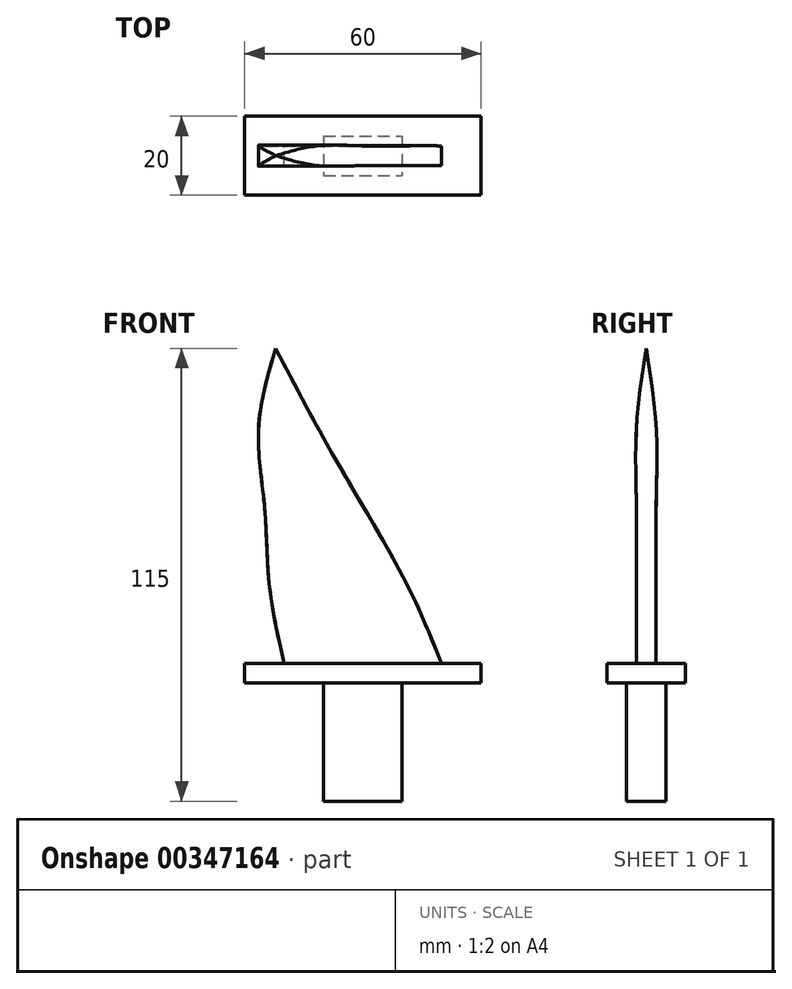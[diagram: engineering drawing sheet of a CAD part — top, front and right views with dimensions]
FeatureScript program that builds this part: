
annotation { "Feature Type Name" : "Feature", "Feature Type Description" : "" }
export const myFeature = defineFeature(function(context is Context, id is Id, definition is map)
    precondition{}
    {
        {
            var Q0;
            Q0=qCreatedBy(makeId("Top.planeOp"),FACE);
            var sketch = newSketch(context, id + "F0", { "sketchPlane" : qUnion([Q0])});
            skLineSegment(sketch, "E0.bottom", {"start": v(-10, 5) * mm, "end": v(10, 5) * mm});
            skLineSegment(sketch, "E0.top", {"start": v(-10, -5) * mm, "end": v(10, -5) * mm});
            skLineSegment(sketch, "E0.left", {"start": v(-10, 5) * mm, "end": v(-10, -5) * mm});
            skLineSegment(sketch, "E0.right", {"start": v(10, 5) * mm, "end": v(10, -5) * mm});
            skPoint(sketch, "E0.middle", {"position": v(0, 0) * mm});
            skSolve(sketch);
        }
        {
            var Q0;
            Q0=makeQuery(id+"F0.imprint","IMPRINT",FACE,{"disambiguationData":[TD([[makeQuery(id+"F0.imprint","IMPRINT",EDGE,{"derivedFrom":sQuery(id+"F0.wireOp",EDGE,"E0.bottom")}),-1.0]])]});
            extrude(context, id + "F1", {"entities" : qUnion([Q0]), "depth" : 30 * mm});
        }
        {
            var Q0;
            Q0=qCreatedBy(makeId("Top.planeOp"),FACE);
            cPlane(context, id + "F2", {"entities" : qUnion([Q0]), "cplaneType" : CPlaneType.OFFSET, "offset" : 30 * mm, "width" : 150 * mm, "height" : 150 * mm});
        }
        {
            var Q0;
            Q0=qCreatedBy(id+"F2.planeOp",FACE);
            var sketch = newSketch(context, id + "F3", { "sketchPlane" : qUnion([Q0])});
            skLineSegment(sketch, "E1.bottom", {"start": v(-30, 10) * mm, "end": v(30, 10) * mm});
            skLineSegment(sketch, "E1.top", {"start": v(-30, -10) * mm, "end": v(30, -10) * mm});
            skLineSegment(sketch, "E1.left", {"start": v(-30, 10) * mm, "end": v(-30, -10) * mm});
            skLineSegment(sketch, "E1.right", {"start": v(30, 10) * mm, "end": v(30, -10) * mm});
            skPoint(sketch, "E1.middle", {"position": v(0, 0) * mm});
            skSolve(sketch);
        }
        {
            var Q0;
            Q0=makeQuery(id+"F3.imprint","IMPRINT",FACE,{"disambiguationData":[TD([[makeQuery(id+"F3.imprint","IMPRINT",EDGE,{"derivedFrom":sQuery(id+"F3.wireOp",EDGE,"E1.bottom")}),-1.0]])]});
            extrude(context, id + "F4", {"entities" : qUnion([Q0]), "operationType" : NewBodyOperationType.ADD, "depth" : 5 * mm});
        }
        {
            var Q0;
            Q0=qCreatedBy(id+"F2.planeOp",FACE);
            cPlane(context, id + "F5", {"entities" : qUnion([Q0]), "cplaneType" : CPlaneType.OFFSET, "offset" : 5 * mm, "width" : 150 * mm, "height" : 150 * mm});
        }
        {
            var Q0;
            Q0=qCreatedBy(id+"F5.planeOp",FACE);
            var sketch = newSketch(context, id + "F6", { "sketchPlane" : qUnion([Q0])});
            skLineSegment(sketch, "E2.bottom", {"start": v(-20, -2.5) * mm, "end": v(20, -2.5) * mm});
            skLineSegment(sketch, "E2.top", {"start": v(-20, 2.5) * mm, "end": v(20, 2.5) * mm});
            skLineSegment(sketch, "E2.left", {"start": v(-20, -2.5) * mm, "end": v(-20, 2.5) * mm});
            skLineSegment(sketch, "E2.right", {"start": v(20, -2.5) * mm, "end": v(20, 2.5) * mm});
            skPoint(sketch, "E2.middle", {"position": v(0, 0) * mm});
            skSolve(sketch);
        }
        {
            var Q0;
            Q0=qCreatedBy(id+"F5.planeOp",FACE);
            cPlane(context, id + "F7", {"entities" : qUnion([Q0]), "cplaneType" : CPlaneType.OFFSET, "offset" : 20 * mm, "width" : 150 * mm, "height" : 150 * mm});
        }
        {
            var Q0;
            Q0=qCreatedBy(id+"F7.planeOp",FACE);
            var sketch = newSketch(context, id + "F8", { "sketchPlane" : qUnion([Q0])});
            skLineSegment(sketch, "E3.bottom", {"start": v(11.25, -2.5) * mm, "end": v(-23.75, -2.5) * mm});
            skLineSegment(sketch, "E3.top", {"start": v(11.25, 2.5) * mm, "end": v(-23.75, 2.5) * mm});
            skLineSegment(sketch, "E3.left", {"start": v(11.25, -2.5) * mm, "end": v(11.25, 2.5) * mm});
            skLineSegment(sketch, "E3.right", {"start": v(-23.75, -2.5) * mm, "end": v(-23.75, 2.5) * mm});
            skPoint(sketch, "E3.middle", {"position": v(-6.25, 0) * mm});
            skSolve(sketch);
        }
        {
            var Q0;
            Q0=qCreatedBy(id+"F7.planeOp",FACE);
            cPlane(context, id + "F9", {"entities" : qUnion([Q0]), "cplaneType" : CPlaneType.OFFSET, "offset" : 20 * mm, "width" : 150 * mm, "height" : 150 * mm});
        }
        {
            var Q0;
            Q0=qCreatedBy(id+"F9.planeOp",FACE);
            var sketch = newSketch(context, id + "F10", { "sketchPlane" : qUnion([Q0])});
            skLineSegment(sketch, "E4.bottom", {"start": v(0, -2.5) * mm, "end": v(-25, -2.5) * mm});
            skLineSegment(sketch, "E4.top", {"start": v(0, 2.5) * mm, "end": v(-25, 2.5) * mm});
            skLineSegment(sketch, "E4.left", {"start": v(0, -2.5) * mm, "end": v(0, 2.5) * mm});
            skLineSegment(sketch, "E4.right", {"start": v(-25, -2.5) * mm, "end": v(-25, 2.5) * mm});
            skPoint(sketch, "E4.middle", {"position": v(-12.5, 0) * mm});
            skSolve(sketch);
        }
        {
            var Q0;
            Q0=qCreatedBy(id+"F9.planeOp",FACE);
            cPlane(context, id + "F11", {"entities" : qUnion([Q0]), "cplaneType" : CPlaneType.OFFSET, "offset" : 20 * mm, "width" : 150 * mm, "height" : 150 * mm});
        }
        {
            var Q0;
            Q0=qCreatedBy(id+"F11.planeOp",FACE);
            var sketch = newSketch(context, id + "F12", { "sketchPlane" : qUnion([Q0])});
            skLineSegment(sketch, "E5.bottom", {"start": v(-26.5, 2.5) * mm, "end": v(-11.5, 2.5) * mm});
            skLineSegment(sketch, "E5.top", {"start": v(-26.5, -2.5) * mm, "end": v(-11.5, -2.5) * mm});
            skLineSegment(sketch, "E5.left", {"start": v(-26.5, 2.5) * mm, "end": v(-26.5, -2.5) * mm});
            skLineSegment(sketch, "E5.right", {"start": v(-11.5, 2.5) * mm, "end": v(-11.5, -2.5) * mm});
            skPoint(sketch, "E5.middle", {"position": v(-19, 0) * mm});
            skSolve(sketch);
        }
        {
            var Q0;
            Q0=qCreatedBy(id+"F11.planeOp",FACE);
            cPlane(context, id + "F13", {"entities" : qUnion([Q0]), "cplaneType" : CPlaneType.OFFSET, "offset" : 20 * mm, "width" : 150 * mm, "height" : 150 * mm});
        }
        {
            var Q0;
            Q0=qCreatedBy(id+"F13.planeOp",FACE);
            var sketch = newSketch(context, id + "F14", { "sketchPlane" : qUnion([Q0])});
            skLineSegment(sketch, "E6.bottom", {"start": v(-23.63, 2.5) * mm, "end": v(-20.63, 2.5) * mm});
            skLineSegment(sketch, "E6.top", {"start": v(-23.63, -2.5) * mm, "end": v(-20.63, -2.5) * mm});
            skLineSegment(sketch, "E6.left", {"start": v(-23.63, 2.5) * mm, "end": v(-23.63, -2.5) * mm});
            skLineSegment(sketch, "E6.right", {"start": v(-20.63, 2.5) * mm, "end": v(-20.63, -2.5) * mm});
            skPoint(sketch, "E6.middle", {"position": v(-22.13, 0) * mm});
            skSolve(sketch);
        }
        {
            var Q1;
            Q1=makeQuery(id+"F6.imprint","IMPRINT",FACE,{"disambiguationData":[TD([[makeQuery(id+"F6.imprint","IMPRINT",EDGE,{"derivedFrom":sQuery(id+"F6.wireOp",EDGE,"E2.bottom")}),1.0]])]});
            var Q2;
            Q2=makeQuery(id+"F8.imprint","IMPRINT",FACE,{"disambiguationData":[TD([[makeQuery(id+"F8.imprint","IMPRINT",EDGE,{"derivedFrom":sQuery(id+"F8.wireOp",EDGE,"E3.bottom")}),-1.0]])]});
            var Q3;
            Q3=makeQuery(id+"F10.imprint","IMPRINT",FACE,{"disambiguationData":[TD([[makeQuery(id+"F10.imprint","IMPRINT",EDGE,{"derivedFrom":sQuery(id+"F10.wireOp",EDGE,"E4.bottom")}),-1.0]])]});
            var Q4;
            Q4=makeQuery(id+"F12.imprint","IMPRINT",FACE,{"disambiguationData":[TD([[makeQuery(id+"F12.imprint","IMPRINT",EDGE,{"derivedFrom":sQuery(id+"F12.wireOp",EDGE,"E5.bottom")}),-1.0]])]});
            var Q5;
            Q5=sQuery(id+"F14.wireOp",VERTEX,"E6.middle");
            loft(context, id + "F15", {"operationType" : NewBodyOperationType.ADD, "sheetProfilesArray" : [{ "sheetProfileEntities" : qUnion([Q1]) }, { "sheetProfileEntities" : qUnion([Q2]) }, { "sheetProfileEntities" : qUnion([Q3]) }, { "sheetProfileEntities" : qUnion([Q4]) }, { "sheetProfileEntities" : qUnion([Q5]) }]});
        }
    });
